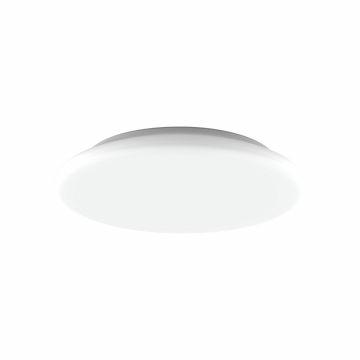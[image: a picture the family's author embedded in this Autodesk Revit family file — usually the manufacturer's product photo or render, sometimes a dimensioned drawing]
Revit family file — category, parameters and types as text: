
# Revit family: Lighting-Terziario-GEWISS-ELIA-CL-LED_PLAFONIERA_TONDA_D250
name_source: partatom
category: Apparecchi per illuminazione
units: mm (PartAtom-declared; Revit-internal decimal feet)

## family parameters
Condiviso = No
Host = Superficie
Punto di calcolo locali = Sì
Quota connettore circolare = Usa diametro
Sorgente d'illuminazione = Sì
Taglio con vuoti quando caricato = No
Tipo di parte = Normale

## types (2) — shared parameters
Angolo inclinazione = -90.00°
Applicazione = Interno
Catalogo = LIGHTING
Catalogo Serie = ELIA CL
Classe isolamento = II
Colore = Bianco
Emetti da lunghezza linea = 610 mm
FORO_CONTROSOFFITTO = 80 mm  [stored 0.262467 ft]
File diagramma fotometrico = GWF1315GA840.IES
Filtro dei colori = 16777215
Garanzia = 5 anni
Grado di protezione = IP20 - IP54
IDF = affa366a-5455-4fea-b1b5-dd73daed3394
IDT = 515d24b2-bb60-4330-99e2-236bf9a850ce
Immagine tipo = ELIA_CL.jpg
Installazione = Plafone - Parete
LARGHEZZA_FORO = 820 mm
LED = <Per categoria>
LED Life time (L80B50) = L80 B50 (Tq25°) = 50.000h
LUNGHEZZA FORO = 969 mm
L_lampada = 1500 mm
Lampada: = LED
Lumen output (lm) = 1150
Ottica = Opale diffondente
POSIZIONE = 80000
Potenza di sistema = 12W
Produttore = GEWISS S.p.A.
Prospetto di default = 1219 mm
Resistenza agli urti = IK08
SEO = Plafone - Parete
STRUTTURA = <Per categoria>
Scheda Tecnica = https://www.gewiss.com
Temperatura di colore = 4000K
Temperatura di colore: = 4000K
Temperatura di funzionamento = -20° +45°
Temperatura di utilizzo = -20° +45°
Tensione = 220-240 VÂ
Tipo lampada = LED
Tipologia = Plafone - Parete
Tipologia sorgente luminosa = LED - Non sostituibile
URL = https://www.gewiss.com
Variazione temperatura colore lampada con luminosità attenuata = <Nessuno>
Versione file RFA = 20.0

## per-type parameters (varying)
| type | Descrizione | Dimensioni (mm) | Modello | Peso (kg) | Peso (kg): |
| GWF1310GA840 - ELIA CL S2 OPAL DIFF 40K ST.ALONE ONOFF | ELIA CL S2 OPAL DIFF 40K ST.ALONE ONOFF | Standard | GWF1310GA840 | 0,5 | 0,5 |
| GWF1315GA840 - ELIA CL S2 OPAL DIFF 40K ST.ALONE MW | ELIA CL S2 OPAL DIFF 40K ST.ALONE MW | Con Sensore / Emergenza | GWF1315GA840 | 0,9 | 0,9 |

note: [stored X ft] marks values corroborated as IEEE doubles in the binary element streams (Revit-internal decimal feet)
